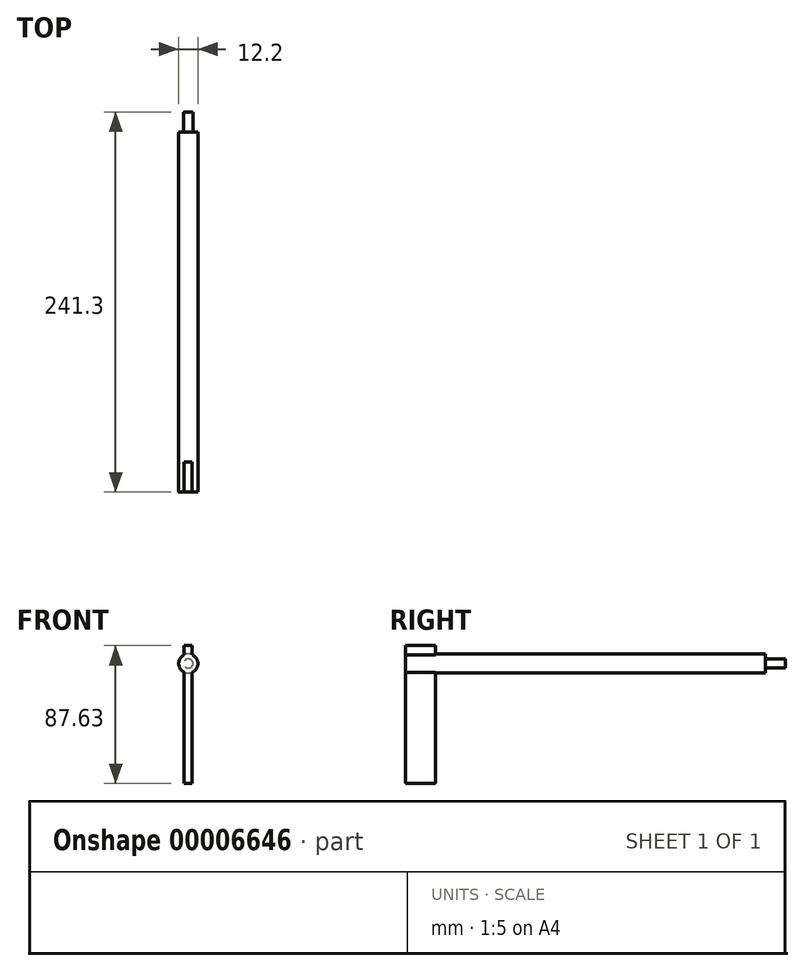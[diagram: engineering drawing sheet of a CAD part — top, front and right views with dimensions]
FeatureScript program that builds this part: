
annotation { "Feature Type Name" : "Feature", "Feature Type Description" : "" }
export const myFeature = defineFeature(function(context is Context, id is Id, definition is map)
    precondition{}
    {
        {
            var Q0;
            Q0=qCreatedBy(makeId("Front.planeOp"),FACE);
            var sketch = newSketch(context, id + "F0", { "sketchPlane" : qUnion([Q0])});
            skCircle(sketch, "E0", {"center": v(0, 0) * mm, "radius": 6.1 * mm});
            skLineSegment(sketch, "E1.bottom", {"start": v(-2.54, 0) * mm, "end": v(2.54, 0) * mm});
            skLineSegment(sketch, "E1.top", {"start": v(-2.54, -76.2) * mm, "end": v(2.54, -76.2) * mm});
            skLineSegment(sketch, "E1.left", {"start": v(-2.54, 0) * mm, "end": v(-2.54, -76.2) * mm});
            skLineSegment(sketch, "E1.right", {"start": v(2.54, 0) * mm, "end": v(2.54, -76.2) * mm});
            skLineSegment(sketch, "E2.bottom", {"start": v(-2.54, 11.43) * mm, "end": v(2.54, 11.43) * mm});
            skLineSegment(sketch, "E2.left", {"start": v(-2.54, 11.43) * mm, "end": v(-2.54, 0) * mm});
            skLineSegment(sketch, "E2.right", {"start": v(2.54, 11.43) * mm, "end": v(2.54, 0) * mm});
            skSolve(sketch);
        }
        {
            var Q0;
            Q0 = qSketchRegion(id + "F0", true);
            extrude(context, id + "F1", {"entities" : qUnion([Q0]), "depth" : 19.05 * mm});
        }
        {
            var Q0;
            Q0=makeQuery(id+"F1.opExtrude","CAP_FACE",FACE,{"disambiguationData":[OSD([sQuery(id+"F0.wireOp",EDGE,"E0"),sQuery(id+"F0.wireOp",EDGE,"E1.top"),sQuery(id+"F0.wireOp",EDGE,"E1.left"),sQuery(id+"F0.wireOp",EDGE,"E1.right"),sQuery(id+"F0.wireOp",EDGE,"E2.bottom"),sQuery(id+"F0.wireOp",EDGE,"E2.left"),sQuery(id+"F0.wireOp",EDGE,"E2.right")])],"isStart":true});
            var sketch = newSketch(context, id + "F2", { "sketchPlane" : qUnion([Q0])});
            skCircle(sketch, "E3", {"center": v(0, 0) * mm, "radius": 6.1 * mm});
            skSolve(sketch);
        }
        {
            var Q0;
            Q0 = qSketchRegion(id + "F2", true);
            extrude(context, id + "F3", {"entities" : qUnion([Q0]), "operationType" : NewBodyOperationType.ADD, "depth" : 209.55 * mm});
        }
        {
            var Q0;
            Q0=makeQuery(id+"F3.opExtrude","CAP_FACE",FACE,{"disambiguationData":[OSD([sQuery(id+"F2.wireOp",EDGE,"E3")])],"isStart":false});
            var sketch = newSketch(context, id + "F4", { "sketchPlane" : qUnion([Q0])});
            skCircle(sketch, "E4", {"center": v(0, 0) * mm, "radius": 2.92 * mm});
            skSolve(sketch);
        }
        {
            var Q0;
            Q0 = qSketchRegion(id + "F4", true);
            extrude(context, id + "F5", {"entities" : qUnion([Q0]), "operationType" : NewBodyOperationType.ADD, "depth" : 12.7 * mm});
        }
    });
